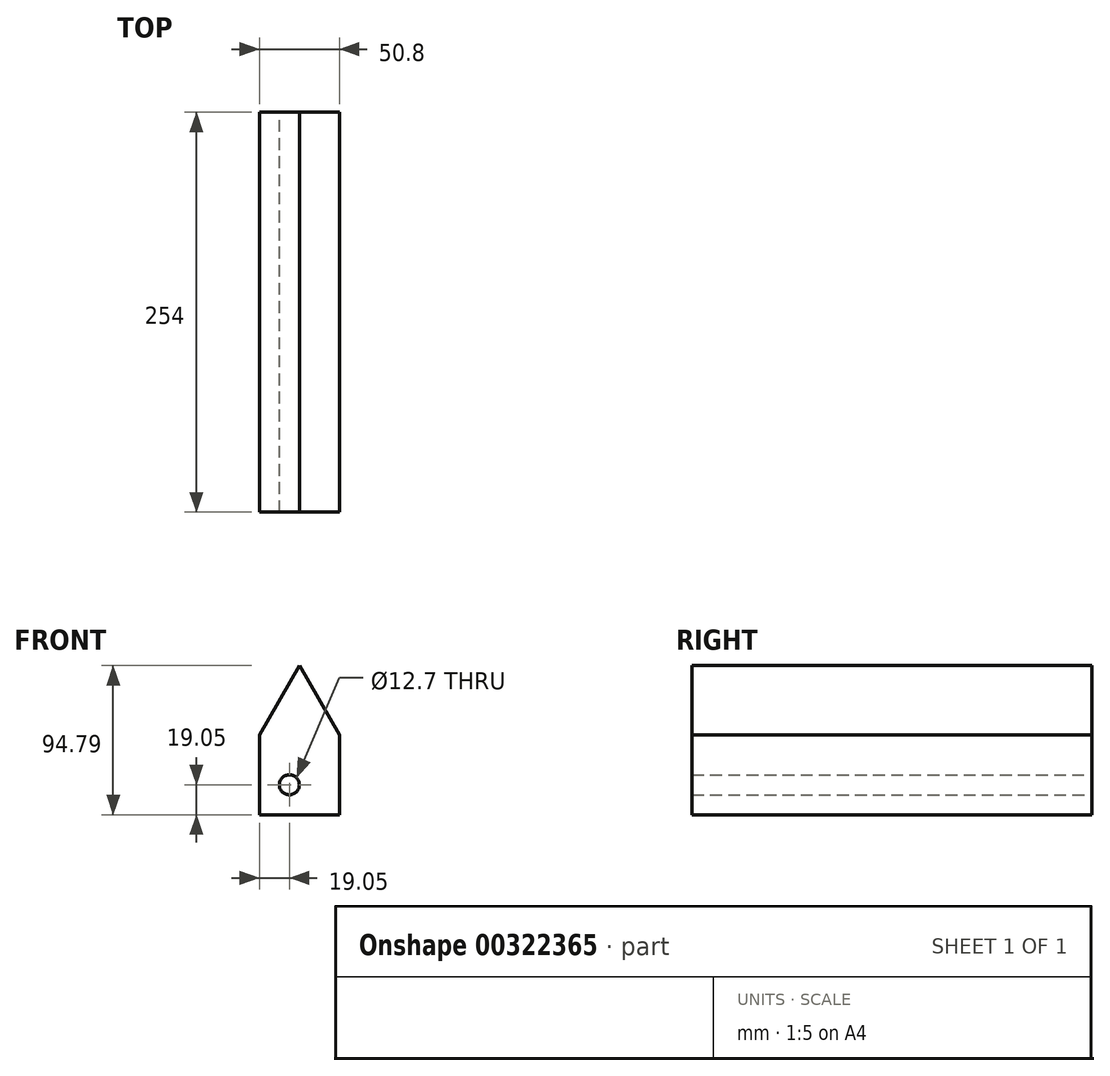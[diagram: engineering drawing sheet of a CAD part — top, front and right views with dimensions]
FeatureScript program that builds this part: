
annotation { "Feature Type Name" : "Feature", "Feature Type Description" : "" }
export const myFeature = defineFeature(function(context is Context, id is Id, definition is map)
    precondition{}
    {
        {
            var Q0;
            Q0=qCreatedBy(makeId("Front.planeOp"),FACE);
            var sketch = newSketch(context, id + "F0", { "sketchPlane" : qUnion([Q0])});
            skLineSegment(sketch, "E0.bottom", {"start": v(25.4, 25.4) * mm, "end": v(-25.4, 25.4) * mm});
            skLineSegment(sketch, "E0.top", {"start": v(25.4, -25.4) * mm, "end": v(-25.4, -25.4) * mm});
            skLineSegment(sketch, "E0.left", {"start": v(25.4, 25.4) * mm, "end": v(25.4, -25.4) * mm});
            skLineSegment(sketch, "E0.right", {"start": v(-25.4, 25.4) * mm, "end": v(-25.4, -25.4) * mm});
            skPoint(sketch, "E0.middle", {"position": v(0, 0) * mm});
            skLineSegment(sketch, "E1", {"start": v(25.4, 25.4) * mm, "end": v(0, 69.4) * mm});
            skLineSegment(sketch, "E2", {"start": v(0, 69.4) * mm, "end": v(-25.4, 25.4) * mm});
            skLineSegment(sketch, "E3.0", {"start": v(25.4, -6.35) * mm, "end": v(-25.4, -6.35) * mm});
            skLineSegment(sketch, "E4.0", {"start": v(-6.35, 25.4) * mm, "end": v(-6.35, -25.4) * mm});
            skCircle(sketch, "E5", {"center": v(-6.35, -6.35) * mm, "radius": 6.35 * mm});
            skPoint(sketch, "E5.centerSnap0", {"position": v(0, -6.35) * mm});
            skSolve(sketch);
        }
        {
            var Q0;
            Q0 = qSketchRegion(id + "F0", true);
            extrude(context, id + "F1", {"entities" : qUnion([Q0]), "depth" : 254 * mm});
        }
    });
